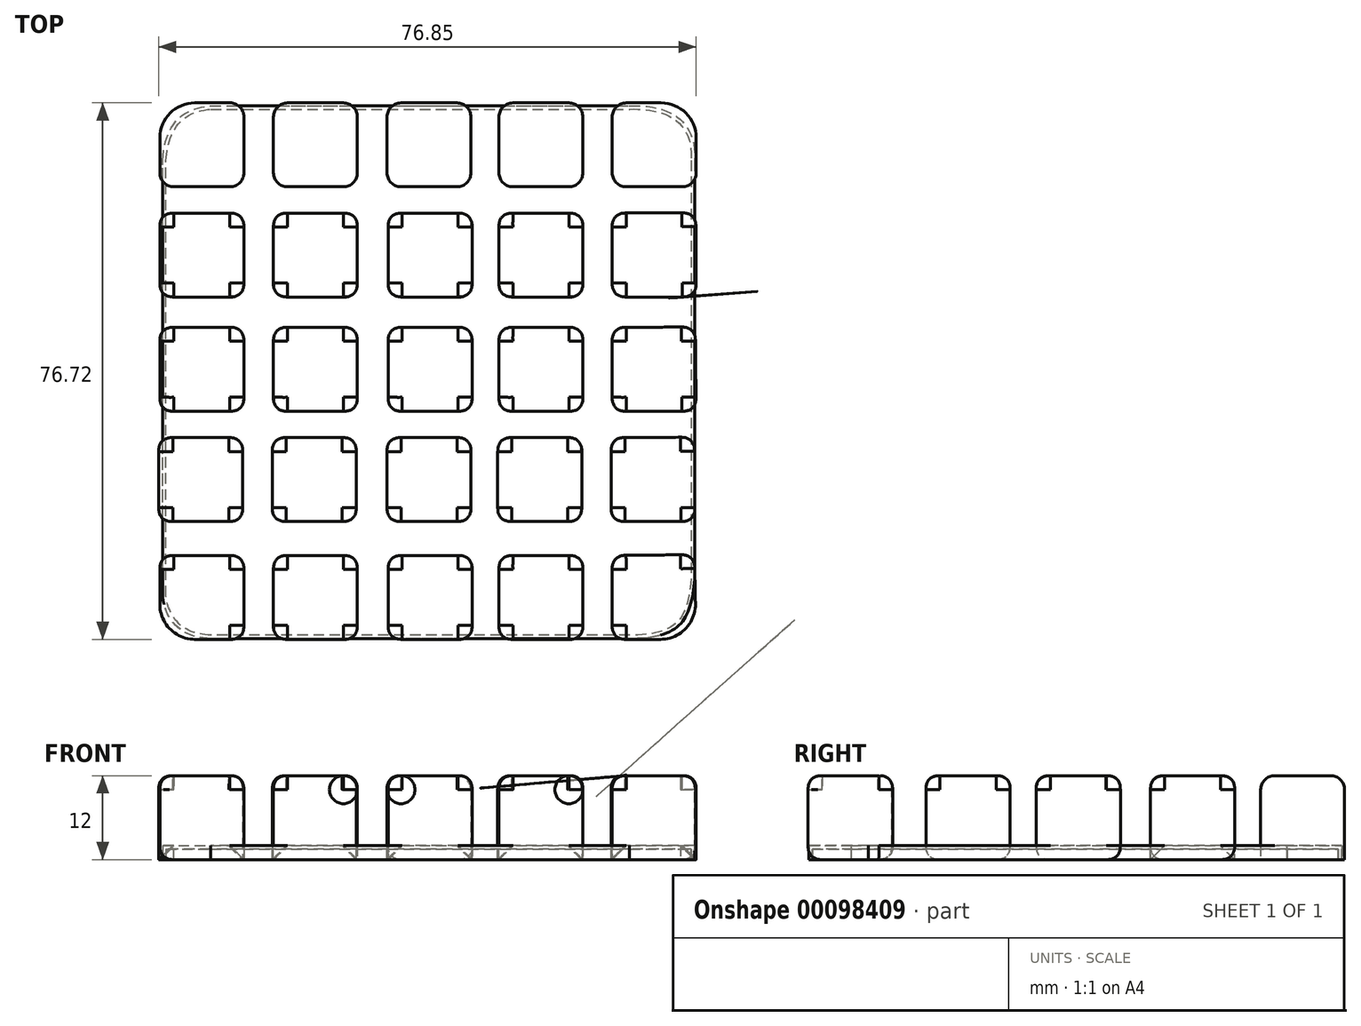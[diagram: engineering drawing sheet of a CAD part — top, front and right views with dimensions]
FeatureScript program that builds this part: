
annotation { "Feature Type Name" : "Feature", "Feature Type Description" : "" }
export const myFeature = defineFeature(function(context is Context, id is Id, definition is map)
    precondition{}
    {
        {
            var Q0;
            Q0=qCreatedBy(makeId("Top.planeOp"),FACE);
            var sketch = newSketch(context, id + "F0", { "sketchPlane" : qUnion([Q0]), "disableImprinting" : false});
            skFitSpline(sketch, "E0", {"points": [v(-42.78, 33) * mm, v(-35.9, 40.85) * mm], "startDerivative": vector(1.12, 17.42) * mm, "endDerivative": vector(10.47, 1.03) * mm});
            skFitSpline(sketch, "E1", {"points": [v(-35.9, 40.85) * mm, v(24.01, 40.85) * mm], "startDerivative": vector(59.63, 0) * mm, "endDerivative": vector(59.63, 0) * mm});
            skFitSpline(sketch, "E2", {"points": [v(24.01, 40.85) * mm, v(33.3, 33) * mm], "startDerivative": vector(21.28, 0.62) * mm, "endDerivative": vector(-0.8, -13.72) * mm});
            skFitSpline(sketch, "E3", {"points": [v(33.3, 33) * mm, v(33.3, -26.83) * mm], "startDerivative": vector(0, -59.82) * mm, "endDerivative": vector(0, -59.82) * mm});
            skFitSpline(sketch, "E4", {"points": [v(33.3, -26.83) * mm, v(24.01, -35.35) * mm], "startDerivative": vector(-1.47, -16.8) * mm, "endDerivative": vector(-22.63, 0.24) * mm});
            skFitSpline(sketch, "E5", {"points": [v(24.01, -35.35) * mm, v(-35.9, -35.35) * mm], "startDerivative": vector(-59.63, 0) * mm, "endDerivative": vector(-59.63, 0) * mm});
            skFitSpline(sketch, "E6", {"points": [v(-35.9, -35.35) * mm, v(-42.78, -29.35) * mm], "startDerivative": vector(-12.8, 0.34) * mm, "endDerivative": vector(-1.44, 10.4) * mm});
            skFitSpline(sketch, "E7", {"points": [v(-42.78, -29.35) * mm, v(-42.78, 33) * mm], "startDerivative": vector(0, 62.34) * mm, "endDerivative": vector(0, 62.34) * mm});
            skLineSegment(sketch, "E8", {"start": v(10.14, 40.85) * mm, "end": v(10.14, -35.35) * mm, "construction": true});
            skSolve(sketch);
        }
        {
            var Q0;
            Q0 = qSketchRegion(id + "F0", true);
            extrude(context, id + "F1", {"entities" : qUnion([Q0]), "depth" : 2 * mm, "offsetDistance" : 25 * mm});
        }
        {
            var Q0;
            Q0=makeQuery(id+"FE2RlGiIe2qTgEf_1.opExtrude","CAP_FACE",FACE,{"disambiguationData":[OSD([sQuery(id+"F0.wireOp",EDGE,"E0"),sQuery(id+"F0.wireOp",EDGE,"E1"),sQuery(id+"F0.wireOp",EDGE,"E2"),sQuery(id+"F0.wireOp",EDGE,"E3"),sQuery(id+"F0.wireOp",EDGE,"E4"),sQuery(id+"F0.wireOp",EDGE,"E5"),sQuery(id+"F0.wireOp",EDGE,"E6"),sQuery(id+"F0.wireOp",EDGE,"E7")])],"isStart":false});
            var Q1;
            Q1=makeQuery(id+"F1.opExtrude","CAP_FACE",FACE,{"disambiguationData":[OSD([sQuery(id+"F0.wireOp",EDGE,"E0"),sQuery(id+"F0.wireOp",EDGE,"E1"),sQuery(id+"F0.wireOp",EDGE,"E2"),sQuery(id+"F0.wireOp",EDGE,"E3"),sQuery(id+"F0.wireOp",EDGE,"E4"),sQuery(id+"F0.wireOp",EDGE,"E5"),sQuery(id+"F0.wireOp",EDGE,"E6"),sQuery(id+"F0.wireOp",EDGE,"E7")])],"isStart":true});
            shell(context, id + "F2", {"entities" : qUnion([Q0, Q1]), "thickness" : 0.5 * mm});
        }
        {
            var Q0;
            Q0=qCreatedBy(makeId("Top.planeOp"),FACE);
            var sketch = newSketch(context, id + "F3", { "sketchPlane" : qUnion([Q0]), "disableImprinting" : false});
            skLineSegment(sketch, "E9.bottom", {"start": v(-38.15, 41.25) * mm, "end": v(-31.13, 41.25) * mm});
            skLineSegment(sketch, "E9.top", {"start": v(-43.15, 29.25) * mm, "end": v(-31.13, 29.25) * mm});
            skLineSegment(sketch, "E9.left", {"start": v(-43.15, 36.25) * mm, "end": v(-43.15, 29.25) * mm});
            skLineSegment(sketch, "E9.right", {"start": v(-31.13, 41.25) * mm, "end": v(-31.13, 29.25) * mm});
            skLineSegment(sketch, "E10.1.0.0", {"start": v(-26.91, 41.25) * mm, "end": v(-14.91, 41.25) * mm});
            skLineSegment(sketch, "E10.1.0.1", {"start": v(-14.91, 41.25) * mm, "end": v(-14.91, 29.25) * mm});
            skLineSegment(sketch, "E10.1.0.2", {"start": v(-26.91, 29.25) * mm, "end": v(-14.91, 29.25) * mm});
            skLineSegment(sketch, "E10.1.0.3", {"start": v(-26.91, 41.25) * mm, "end": v(-26.91, 29.25) * mm});
            skLineSegment(sketch, "E10.2.0.0", {"start": v(-10.67, 41.25) * mm, "end": v(1.33, 41.25) * mm});
            skLineSegment(sketch, "E10.2.0.1", {"start": v(1.33, 41.25) * mm, "end": v(1.33, 29.25) * mm});
            skLineSegment(sketch, "E10.2.0.2", {"start": v(-10.67, 29.25) * mm, "end": v(1.33, 29.25) * mm});
            skLineSegment(sketch, "E10.2.0.3", {"start": v(-10.67, 41.25) * mm, "end": v(-10.67, 29.25) * mm});
            skLineSegment(sketch, "E10.3.0.0", {"start": v(5.33, 41.25) * mm, "end": v(17.33, 41.25) * mm});
            skLineSegment(sketch, "E10.3.0.1", {"start": v(17.33, 41.25) * mm, "end": v(17.33, 29.25) * mm});
            skLineSegment(sketch, "E10.3.0.2", {"start": v(5.33, 29.25) * mm, "end": v(17.33, 29.25) * mm});
            skLineSegment(sketch, "E10.3.0.3", {"start": v(5.33, 41.25) * mm, "end": v(5.33, 29.25) * mm});
            skLineSegment(sketch, "E10.4.0.0", {"start": v(21.53, 41.25) * mm, "end": v(28.53, 41.25) * mm});
            skLineSegment(sketch, "E10.4.0.1", {"start": v(33.53, 36.25) * mm, "end": v(33.53, 29.25) * mm});
            skLineSegment(sketch, "E10.4.0.2", {"start": v(21.53, 29.25) * mm, "end": v(33.53, 29.25) * mm});
            skLineSegment(sketch, "E10.4.0.3", {"start": v(21.53, 41.25) * mm, "end": v(21.53, 29.25) * mm});
            skPoint(sketch, "E11.visualSharp", {"position": v(35.33, 41.25) * mm});
            skArc(sketch, "E11.filletArc", {"start": v(33.53, 36.25) * mm, "mid": v(32.06, 39.79) * mm, "end": v(28.53, 41.25) * mm});
            skLineSegment(sketch, "E12.bottom", {"start": v(-43.15, 25.5) * mm, "end": v(-31.15, 25.5) * mm});
            skLineSegment(sketch, "E12.top", {"start": v(-43.15, 13.5) * mm, "end": v(-31.15, 13.5) * mm});
            skLineSegment(sketch, "E12.left", {"start": v(-43.15, 25.5) * mm, "end": v(-43.15, 13.5) * mm});
            skLineSegment(sketch, "E12.right", {"start": v(-31.15, 25.5) * mm, "end": v(-31.15, 13.5) * mm});
            skLineSegment(sketch, "E13.1.0.0", {"start": v(-26.91, 25.5) * mm, "end": v(-14.91, 25.5) * mm});
            skLineSegment(sketch, "E13.1.0.1", {"start": v(-14.91, 25.5) * mm, "end": v(-14.91, 13.5) * mm});
            skLineSegment(sketch, "E13.1.0.2", {"start": v(-26.91, 13.5) * mm, "end": v(-14.91, 13.5) * mm});
            skLineSegment(sketch, "E13.1.0.3", {"start": v(-26.91, 25.5) * mm, "end": v(-26.91, 13.5) * mm});
            skLineSegment(sketch, "E13.2.0.0", {"start": v(-10.51, 25.5) * mm, "end": v(1.49, 25.5) * mm});
            skLineSegment(sketch, "E13.2.0.1", {"start": v(1.49, 25.5) * mm, "end": v(1.49, 13.5) * mm});
            skLineSegment(sketch, "E13.2.0.2", {"start": v(-10.51, 13.5) * mm, "end": v(1.49, 13.5) * mm});
            skLineSegment(sketch, "E13.2.0.3", {"start": v(-10.51, 25.5) * mm, "end": v(-10.51, 13.5) * mm});
            skLineSegment(sketch, "E13.3.0.0", {"start": v(5.33, 25.5) * mm, "end": v(17.33, 25.5) * mm});
            skLineSegment(sketch, "E13.3.0.1", {"start": v(17.33, 25.5) * mm, "end": v(17.33, 13.5) * mm});
            skLineSegment(sketch, "E13.3.0.2", {"start": v(5.33, 13.5) * mm, "end": v(17.33, 13.5) * mm});
            skLineSegment(sketch, "E13.3.0.3", {"start": v(5.33, 25.5) * mm, "end": v(5.33, 13.5) * mm});
            skLineSegment(sketch, "E13.4.0.0", {"start": v(21.53, 25.5) * mm, "end": v(33.48, 25.53) * mm});
            skLineSegment(sketch, "E13.4.0.1", {"start": v(33.48, 25.53) * mm, "end": v(33.53, 13.5) * mm});
            skLineSegment(sketch, "E13.4.0.2", {"start": v(21.53, 13.5) * mm, "end": v(33.53, 13.5) * mm});
            skLineSegment(sketch, "E13.4.0.3", {"start": v(21.53, 25.5) * mm, "end": v(21.53, 13.5) * mm});
            skLineSegment(sketch, "E14.bottom", {"start": v(-43.15, 9.15) * mm, "end": v(-31.15, 9.15) * mm});
            skLineSegment(sketch, "E14.top", {"start": v(-43.15, -2.85) * mm, "end": v(-31.15, -2.85) * mm});
            skLineSegment(sketch, "E14.left", {"start": v(-43.15, 9.15) * mm, "end": v(-43.15, -2.85) * mm});
            skLineSegment(sketch, "E14.right", {"start": v(-31.15, 9.15) * mm, "end": v(-31.15, -2.85) * mm});
            skLineSegment(sketch, "E15.1.0.0", {"start": v(-26.91, 9.15) * mm, "end": v(-14.91, 9.15) * mm});
            skLineSegment(sketch, "E15.1.0.1", {"start": v(-14.91, 9.15) * mm, "end": v(-14.91, -2.85) * mm});
            skLineSegment(sketch, "E15.1.0.2", {"start": v(-26.91, -2.85) * mm, "end": v(-14.91, -2.85) * mm});
            skLineSegment(sketch, "E15.1.0.3", {"start": v(-26.91, 9.15) * mm, "end": v(-26.91, -2.85) * mm});
            skLineSegment(sketch, "E15.2.0.0", {"start": v(-10.51, 9.15) * mm, "end": v(1.49, 9.15) * mm});
            skLineSegment(sketch, "E15.2.0.1", {"start": v(1.49, 9.15) * mm, "end": v(1.49, -2.85) * mm});
            skLineSegment(sketch, "E15.2.0.2", {"start": v(-10.51, -2.85) * mm, "end": v(1.49, -2.85) * mm});
            skLineSegment(sketch, "E15.2.0.3", {"start": v(-10.51, 9.15) * mm, "end": v(-10.51, -2.85) * mm});
            skLineSegment(sketch, "E15.3.0.0", {"start": v(5.33, 9.15) * mm, "end": v(17.33, 9.15) * mm});
            skLineSegment(sketch, "E15.3.0.1", {"start": v(17.33, 9.15) * mm, "end": v(17.33, -2.85) * mm});
            skLineSegment(sketch, "E15.3.0.2", {"start": v(5.33, -2.85) * mm, "end": v(17.33, -2.85) * mm});
            skLineSegment(sketch, "E15.3.0.3", {"start": v(5.33, 9.15) * mm, "end": v(5.33, -2.85) * mm});
            skLineSegment(sketch, "E15.4.0.0", {"start": v(21.53, 9.15) * mm, "end": v(33.4, 9.2) * mm});
            skLineSegment(sketch, "E15.4.0.1", {"start": v(33.4, 9.2) * mm, "end": v(33.53, -2.85) * mm});
            skLineSegment(sketch, "E15.4.0.2", {"start": v(21.53, -2.85) * mm, "end": v(33.53, -2.85) * mm});
            skLineSegment(sketch, "E15.4.0.3", {"start": v(21.53, 9.15) * mm, "end": v(21.53, -2.85) * mm});
            skLineSegment(sketch, "E16.bottom", {"start": v(-43.31, -6.62) * mm, "end": v(-31.31, -6.62) * mm});
            skLineSegment(sketch, "E16.top", {"start": v(-43.31, -18.62) * mm, "end": v(-31.31, -18.62) * mm});
            skLineSegment(sketch, "E16.left", {"start": v(-43.31, -6.62) * mm, "end": v(-43.31, -18.62) * mm});
            skLineSegment(sketch, "E16.right", {"start": v(-31.31, -6.62) * mm, "end": v(-31.31, -18.62) * mm});
            skLineSegment(sketch, "E17.1.0.0", {"start": v(-27.07, -6.62) * mm, "end": v(-15.07, -6.62) * mm});
            skLineSegment(sketch, "E17.1.0.1", {"start": v(-15.07, -6.62) * mm, "end": v(-15.07, -18.62) * mm});
            skLineSegment(sketch, "E17.1.0.2", {"start": v(-27.07, -18.62) * mm, "end": v(-15.07, -18.62) * mm});
            skLineSegment(sketch, "E17.1.0.3", {"start": v(-27.07, -6.62) * mm, "end": v(-27.07, -18.62) * mm});
            skLineSegment(sketch, "E17.2.0.0", {"start": v(-10.67, -6.62) * mm, "end": v(1.33, -6.62) * mm});
            skLineSegment(sketch, "E17.2.0.1", {"start": v(1.33, -6.62) * mm, "end": v(1.33, -18.62) * mm});
            skLineSegment(sketch, "E17.2.0.2", {"start": v(-10.67, -18.62) * mm, "end": v(1.33, -18.62) * mm});
            skLineSegment(sketch, "E17.2.0.3", {"start": v(-10.67, -6.62) * mm, "end": v(-10.67, -18.62) * mm});
            skLineSegment(sketch, "E17.3.0.0", {"start": v(5.16, -6.62) * mm, "end": v(17.16, -6.62) * mm});
            skLineSegment(sketch, "E17.3.0.1", {"start": v(17.16, -6.62) * mm, "end": v(17.16, -18.62) * mm});
            skLineSegment(sketch, "E17.3.0.2", {"start": v(5.16, -18.62) * mm, "end": v(17.16, -18.62) * mm});
            skLineSegment(sketch, "E17.3.0.3", {"start": v(5.16, -6.62) * mm, "end": v(5.16, -18.62) * mm});
            skLineSegment(sketch, "E17.4.0.0", {"start": v(21.36, -6.62) * mm, "end": v(33.28, -6.56) * mm});
            skLineSegment(sketch, "E17.4.0.1", {"start": v(33.28, -6.56) * mm, "end": v(33.36, -18.62) * mm});
            skLineSegment(sketch, "E17.4.0.2", {"start": v(21.36, -18.62) * mm, "end": v(33.36, -18.62) * mm});
            skLineSegment(sketch, "E17.4.0.3", {"start": v(21.36, -6.62) * mm, "end": v(21.36, -18.62) * mm});
            skLineSegment(sketch, "E18.bottom", {"start": v(-43.15, -23.47) * mm, "end": v(-31.15, -23.47) * mm});
            skLineSegment(sketch, "E18.top", {"start": v(-38.15, -35.47) * mm, "end": v(-31.15, -35.47) * mm});
            skLineSegment(sketch, "E18.left", {"start": v(-43.15, -23.47) * mm, "end": v(-43.15, -30.47) * mm});
            skLineSegment(sketch, "E18.right", {"start": v(-31.15, -23.47) * mm, "end": v(-31.15, -35.47) * mm});
            skLineSegment(sketch, "E19.1.0.0", {"start": v(-26.91, -23.47) * mm, "end": v(-14.91, -23.47) * mm});
            skLineSegment(sketch, "E19.1.0.1", {"start": v(-14.91, -23.47) * mm, "end": v(-14.91, -35.47) * mm});
            skLineSegment(sketch, "E19.1.0.2", {"start": v(-26.91, -35.47) * mm, "end": v(-14.91, -35.47) * mm});
            skLineSegment(sketch, "E19.1.0.3", {"start": v(-26.91, -23.47) * mm, "end": v(-26.91, -35.47) * mm});
            skLineSegment(sketch, "E19.2.0.0", {"start": v(-10.51, -23.47) * mm, "end": v(1.49, -23.47) * mm});
            skLineSegment(sketch, "E19.2.0.1", {"start": v(1.49, -23.47) * mm, "end": v(1.49, -35.47) * mm});
            skLineSegment(sketch, "E19.2.0.2", {"start": v(-10.51, -35.47) * mm, "end": v(1.49, -35.47) * mm});
            skLineSegment(sketch, "E19.2.0.3", {"start": v(-10.51, -23.47) * mm, "end": v(-10.51, -35.47) * mm});
            skLineSegment(sketch, "E19.3.0.0", {"start": v(5.33, -23.47) * mm, "end": v(17.33, -23.47) * mm});
            skLineSegment(sketch, "E19.3.0.1", {"start": v(17.33, -23.47) * mm, "end": v(17.33, -35.47) * mm});
            skLineSegment(sketch, "E19.3.0.2", {"start": v(5.33, -35.47) * mm, "end": v(17.33, -35.47) * mm});
            skLineSegment(sketch, "E19.3.0.3", {"start": v(5.33, -23.47) * mm, "end": v(5.33, -35.47) * mm});
            skLineSegment(sketch, "E19.4.0.0", {"start": v(21.53, -23.47) * mm, "end": v(33.28, -23.36) * mm});
            skLineSegment(sketch, "E19.4.0.1", {"start": v(33.28, -23.36) * mm, "end": v(33.42, -30.37) * mm});
            skLineSegment(sketch, "E19.4.0.2", {"start": v(21.53, -35.47) * mm, "end": v(28.42, -35.47) * mm});
            skLineSegment(sketch, "E19.4.0.3", {"start": v(21.53, -23.47) * mm, "end": v(21.53, -35.47) * mm});
            skPoint(sketch, "E20.newPointA", {"position": v(-44.7, 41.25) * mm});
            skPoint(sketch, "E20.newPointB", {"position": v(-44.7, 41.25) * mm});
            skArc(sketch, "E20.filletArc", {"start": v(-38.15, 41.25) * mm, "mid": v(-41.69, 39.79) * mm, "end": v(-43.15, 36.25) * mm});
            skPoint(sketch, "E21.visualSharp", {"position": v(-44.51, -35.47) * mm});
            skArc(sketch, "E21.filletArc", {"start": v(-43.15, -30.47) * mm, "mid": v(-41.69, -34) * mm, "end": v(-38.15, -35.47) * mm});
            skPoint(sketch, "E22.visualSharp", {"position": v(33.53, -35.47) * mm});
            skArc(sketch, "E22.filletArc", {"start": v(28.42, -35.47) * mm, "mid": v(32, -33.97) * mm, "end": v(33.42, -30.37) * mm});
            skLineSegment(sketch, "E23", {"start": v(-48.6, 32.93) * mm, "end": v(-43.15, 32.93) * mm, "construction": true});
            skSolve(sketch);
        }
        {
            var Q0;
            Q0 = qSketchRegion(id + "F3", true);
            extrude(context, id + "F4", {"entities" : qUnion([Q0]), "depth" : 12 * mm, "offsetDistance" : 25 * mm});
        }
        {
            var Q0;
            Q0=makeQuery(id+"F4.opExtrude","CAP_EDGE",EDGE,{"disambiguationData":[OSD([sQuery(id+"F3.wireOp",EDGE,"E10.2.0.3")])],"isStart":false});
            var Q1;
            Q1=makeQuery(id+"F4.opExtrude","CAP_EDGE",EDGE,{"disambiguationData":[OSD([sQuery(id+"F3.wireOp",EDGE,"E10.2.0.1")])],"isStart":false});
            var Q2;
            Q2=makeQuery(id+"F4.opExtrude","CAP_EDGE",EDGE,{"disambiguationData":[OSD([sQuery(id+"F3.wireOp",EDGE,"E10.1.0.1")])],"isStart":false});
            var Q3;
            Q3=makeQuery(id+"F4.opExtrude","CAP_EDGE",EDGE,{"disambiguationData":[OSD([sQuery(id+"F3.wireOp",EDGE,"E10.1.0.3")])],"isStart":false});
            var Q4;
            Q4=makeQuery(id+"F4.opExtrude","CAP_EDGE",EDGE,{"disambiguationData":[OSD([sQuery(id+"F3.wireOp",EDGE,"E10.3.0.3")])],"isStart":false});
            var Q5;
            Q5=makeQuery(id+"F4.opExtrude","CAP_EDGE",EDGE,{"disambiguationData":[OSD([sQuery(id+"F3.wireOp",EDGE,"E10.3.0.1")])],"isStart":false});
            var Q6;
            Q6=makeQuery(id+"F4.opExtrude","CAP_EDGE",EDGE,{"disambiguationData":[OSD([sQuery(id+"F3.wireOp",EDGE,"E9.right")])],"isStart":false});
            var Q7;
            Q7=makeQuery(id+"F4.opExtrude","CAP_EDGE",EDGE,{"disambiguationData":[OSD([sQuery(id+"F3.wireOp",EDGE,"E10.4.0.3")])],"isStart":false});
            var Q8;
            Q8=makeQuery(id+"F4.opExtrude","CAP_EDGE",EDGE,{"disambiguationData":[OSD([sQuery(id+"F3.wireOp",EDGE,"E9.left")])],"isStart":false});
            var Q9;
            Q9=makeQuery(id+"F4.opExtrude","CAP_EDGE",EDGE,{"disambiguationData":[OSD([sQuery(id+"F3.wireOp",EDGE,"E10.4.0.1")])],"isStart":false});
            fillet(context, id + "F5", {"entities" : qUnion([Q0, Q1, Q2, Q3, Q4, Q5, Q6, Q7, Q8, Q9]), "tangentPropagation" : true, "radius" : 2 * mm, "defaultsChanged" : false, "vertexSettings" : [], "allowEdgeOverflow" : false});
        }
        {
            var Q0;
            Q0=makeQuery(id+"F4.opExtrude","CAP_EDGE",EDGE,{"disambiguationData":[OSD([sQuery(id+"F3.wireOp",EDGE,"E9.top")])],"isStart":false});
            fillet(context, id + "F6", {"entities" : qUnion([Q0]), "tangentPropagation" : true, "radius" : 2 * mm, "defaultsChanged" : true, "vertexSettings" : [], "allowEdgeOverflow" : false});
        }
        {
            var Q0;
            Q0=makeQuery(id+"F4.opExtrude","CAP_EDGE",EDGE,{"disambiguationData":[OSD([sQuery(id+"F3.wireOp",EDGE,"E10.1.0.2")])],"isStart":false});
            var Q1;
            Q1=makeQuery(id+"F4.opExtrude","CAP_EDGE",EDGE,{"disambiguationData":[OSD([sQuery(id+"F3.wireOp",EDGE,"E10.2.0.2")])],"isStart":false});
            var Q2;
            Q2=makeQuery(id+"F5.opFillet","BLEND_EDGE",EDGE,{"blendedFrom":[makeQuery(id+"F4.opExtrude","CAP_EDGE",EDGE,{"disambiguationData":[OSD([sQuery(id+"F3.wireOp",EDGE,"E10.1.0.1")])],"isStart":false}),makeQuery(id+"F4.opExtrude","SWEPT_FACE",FACE,{"disambiguationData":[OSD([sQuery(id+"F3.wireOp",EDGE,"E10.1.0.2")])]})],"blendedInto":[makeQuery(id+"F4.opExtrude","SWEPT_FACE",FACE,{"disambiguationData":[OSD([sQuery(id+"F3.wireOp",EDGE,"E10.1.0.2")])]})]});
            var Q3;
            Q3=makeQuery(id+"F5.opFillet","BLEND_EDGE",EDGE,{"blendedFrom":[makeQuery(id+"F4.opExtrude","CAP_EDGE",EDGE,{"disambiguationData":[OSD([sQuery(id+"F3.wireOp",EDGE,"E10.1.0.3")])],"isStart":false}),makeQuery(id+"F4.opExtrude","SWEPT_FACE",FACE,{"disambiguationData":[OSD([sQuery(id+"F3.wireOp",EDGE,"E10.1.0.2")])]})],"blendedInto":[makeQuery(id+"F4.opExtrude","SWEPT_FACE",FACE,{"disambiguationData":[OSD([sQuery(id+"F3.wireOp",EDGE,"E10.1.0.2")])]})]});
            var Q4;
            Q4=makeQuery(id+"F4.opExtrude","CAP_EDGE",EDGE,{"disambiguationData":[OSD([sQuery(id+"F3.wireOp",EDGE,"E10.1.0.0")])],"isStart":false});
            var Q5;
            Q5=makeQuery(id+"F4.opExtrude","CAP_EDGE",EDGE,{"disambiguationData":[OSD([sQuery(id+"F3.wireOp",EDGE,"E10.2.0.0")])],"isStart":false});
            var Q6;
            Q6=makeQuery(id+"F4.opExtrude","CAP_EDGE",EDGE,{"disambiguationData":[OSD([sQuery(id+"F3.wireOp",EDGE,"E10.3.0.0")])],"isStart":false});
            var Q7;
            Q7=makeQuery(id+"F4.opExtrude","CAP_EDGE",EDGE,{"disambiguationData":[OSD([sQuery(id+"F3.wireOp",EDGE,"E10.3.0.2")])],"isStart":false});
            var Q8;
            Q8=makeQuery(id+"F4.opExtrude","CAP_EDGE",EDGE,{"disambiguationData":[OSD([sQuery(id+"F3.wireOp",EDGE,"E10.4.0.2")])],"isStart":false});
            var Q9;
            {var subQ0=sQuery(id+"F3.wireOp",EDGE,"E10.4.0.0");Q9=makeQuery(id+"F5.opFillet","BLEND_EDGE",EDGE,{"blendedFrom":[makeQuery(id+"F4.opExtrude","CAP_EDGE",EDGE,{"disambiguationData":[OSD([subQ0])],"isStart":false}),makeQuery(id+"F4.opExtrude","CAP_FACE",FACE,{"disambiguationData":[OSD([subQ0,sQuery(id+"F3.wireOp",EDGE,"E10.4.0.1"),sQuery(id+"F3.wireOp",EDGE,"E10.4.0.2"),sQuery(id+"F3.wireOp",EDGE,"E10.4.0.3"),sQuery(id+"F3.wireOp",EDGE,"E11.filletArc")])],"isStart":false})],"blendedInto":[makeQuery(id+"F4.opExtrude","CAP_FACE",FACE,{"disambiguationData":[OSD([subQ0,sQuery(id+"F3.wireOp",EDGE,"E10.4.0.1"),sQuery(id+"F3.wireOp",EDGE,"E10.4.0.2"),sQuery(id+"F3.wireOp",EDGE,"E10.4.0.3"),sQuery(id+"F3.wireOp",EDGE,"E11.filletArc")])],"isStart":false})]});}
            var Q10;
            Q10=makeQuery(id+"F5.opFillet","BLEND_FACE",FACE,{"disambiguationData":[OSD([sQuery(id+"F3.wireOp",EDGE,"E10.4.0.0")])]});
            var Q11;
            Q11=makeQuery(id+"F5.opFillet","BLEND_FACE",FACE,{"disambiguationData":[OSD([sQuery(id+"F3.wireOp",EDGE,"E9.bottom")])]});
            fillet(context, id + "F7", {"entities" : qUnion([Q0, Q1, Q2, Q3, Q4, Q5, Q6, Q7, Q8, Q9, Q10, Q11]), "tangentPropagation" : true, "radius" : 2 * mm, "defaultsChanged" : false, "vertexSettings" : [], "allowEdgeOverflow" : false});
        }
        {
            var Q0;
            Q0=makeQuery(id+"F4.opExtrude","CAP_EDGE",EDGE,{"disambiguationData":[OSD([sQuery(id+"F3.wireOp",EDGE,"E13.1.0.0")])],"isStart":false});
            var Q1;
            Q1=makeQuery(id+"F4.opExtrude","CAP_EDGE",EDGE,{"disambiguationData":[OSD([sQuery(id+"F3.wireOp",EDGE,"E13.1.0.1")])],"isStart":false});
            var Q2;
            Q2=makeQuery(id+"F4.opExtrude","CAP_EDGE",EDGE,{"disambiguationData":[OSD([sQuery(id+"F3.wireOp",EDGE,"E13.1.0.2")])],"isStart":false});
            var Q3;
            Q3=makeQuery(id+"F4.opExtrude","CAP_EDGE",EDGE,{"disambiguationData":[OSD([sQuery(id+"F3.wireOp",EDGE,"E13.1.0.3")])],"isStart":false});
            var Q4;
            Q4=makeQuery(id+"F4.opExtrude","SWEPT_FACE",FACE,{"disambiguationData":[OSD([sQuery(id+"F3.wireOp",EDGE,"E13.1.0.0")])]});
            var Q5;
            Q5=makeQuery(id+"F4.opExtrude","SWEPT_FACE",FACE,{"disambiguationData":[OSD([sQuery(id+"F3.wireOp",EDGE,"E13.1.0.2")])]});
            var Q6;
            Q6=makeQuery(id+"F4.opExtrude","CAP_EDGE",EDGE,{"disambiguationData":[OSD([sQuery(id+"F3.wireOp",EDGE,"E13.2.0.2")])],"isStart":false});
            var Q7;
            Q7=makeQuery(id+"F4.opExtrude","CAP_EDGE",EDGE,{"disambiguationData":[OSD([sQuery(id+"F3.wireOp",EDGE,"E13.2.0.1")])],"isStart":false});
            var Q8;
            Q8=makeQuery(id+"F4.opExtrude","CAP_EDGE",EDGE,{"disambiguationData":[OSD([sQuery(id+"F3.wireOp",EDGE,"E13.2.0.0")])],"isStart":false});
            var Q9;
            Q9=makeQuery(id+"F4.opExtrude","CAP_EDGE",EDGE,{"disambiguationData":[OSD([sQuery(id+"F3.wireOp",EDGE,"E13.2.0.3")])],"isStart":false});
            var Q10;
            Q10=makeQuery(id+"F4.opExtrude","SWEPT_FACE",FACE,{"disambiguationData":[OSD([sQuery(id+"F3.wireOp",EDGE,"E13.2.0.3")])]});
            var Q11;
            Q11=makeQuery(id+"F4.opExtrude","SWEPT_FACE",FACE,{"disambiguationData":[OSD([sQuery(id+"F3.wireOp",EDGE,"E13.2.0.1")])]});
            var Q12;
            Q12=makeQuery(id+"F4.opExtrude","CAP_FACE",FACE,{"disambiguationData":[OSD([sQuery(id+"F3.wireOp",EDGE,"E13.3.0.0"),sQuery(id+"F3.wireOp",EDGE,"E13.3.0.1"),sQuery(id+"F3.wireOp",EDGE,"E13.3.0.2"),sQuery(id+"F3.wireOp",EDGE,"E13.3.0.3")])],"isStart":false});
            var Q13;
            Q13=makeQuery(id+"F4.opExtrude","CAP_FACE",FACE,{"disambiguationData":[OSD([sQuery(id+"F3.wireOp",EDGE,"E13.4.0.0"),sQuery(id+"F3.wireOp",EDGE,"E13.4.0.1"),sQuery(id+"F3.wireOp",EDGE,"E13.4.0.2"),sQuery(id+"F3.wireOp",EDGE,"E13.4.0.3")])],"isStart":false});
            var Q14;
            Q14=makeQuery(id+"F4.opExtrude","CAP_FACE",FACE,{"disambiguationData":[OSD([sQuery(id+"F3.wireOp",EDGE,"E12.bottom"),sQuery(id+"F3.wireOp",EDGE,"E12.top"),sQuery(id+"F3.wireOp",EDGE,"E12.left"),sQuery(id+"F3.wireOp",EDGE,"E12.right")])],"isStart":false});
            var Q15;
            Q15=makeQuery(id+"F4.opExtrude","CAP_FACE",FACE,{"disambiguationData":[OSD([sQuery(id+"F3.wireOp",EDGE,"E14.bottom"),sQuery(id+"F3.wireOp",EDGE,"E14.top"),sQuery(id+"F3.wireOp",EDGE,"E14.left"),sQuery(id+"F3.wireOp",EDGE,"E14.right")])],"isStart":false});
            var Q16;
            Q16=makeQuery(id+"F4.opExtrude","CAP_FACE",FACE,{"disambiguationData":[OSD([sQuery(id+"F3.wireOp",EDGE,"E15.1.0.0"),sQuery(id+"F3.wireOp",EDGE,"E15.1.0.1"),sQuery(id+"F3.wireOp",EDGE,"E15.1.0.2"),sQuery(id+"F3.wireOp",EDGE,"E15.1.0.3")])],"isStart":false});
            var Q17;
            Q17=makeQuery(id+"F4.opExtrude","CAP_FACE",FACE,{"disambiguationData":[OSD([sQuery(id+"F3.wireOp",EDGE,"E15.2.0.0"),sQuery(id+"F3.wireOp",EDGE,"E15.2.0.1"),sQuery(id+"F3.wireOp",EDGE,"E15.2.0.2"),sQuery(id+"F3.wireOp",EDGE,"E15.2.0.3")])],"isStart":false});
            var Q18;
            Q18=makeQuery(id+"F4.opExtrude","CAP_FACE",FACE,{"disambiguationData":[OSD([sQuery(id+"F3.wireOp",EDGE,"E15.3.0.0"),sQuery(id+"F3.wireOp",EDGE,"E15.3.0.1"),sQuery(id+"F3.wireOp",EDGE,"E15.3.0.2"),sQuery(id+"F3.wireOp",EDGE,"E15.3.0.3")])],"isStart":false});
            var Q19;
            Q19=makeQuery(id+"F4.opExtrude","CAP_FACE",FACE,{"disambiguationData":[OSD([sQuery(id+"F3.wireOp",EDGE,"E15.4.0.0"),sQuery(id+"F3.wireOp",EDGE,"E15.4.0.1"),sQuery(id+"F3.wireOp",EDGE,"E15.4.0.2"),sQuery(id+"F3.wireOp",EDGE,"E15.4.0.3")])],"isStart":false});
            var Q20;
            Q20=makeQuery(id+"F4.opExtrude","CAP_FACE",FACE,{"disambiguationData":[OSD([sQuery(id+"F3.wireOp",EDGE,"E17.4.0.0"),sQuery(id+"F3.wireOp",EDGE,"E17.4.0.1"),sQuery(id+"F3.wireOp",EDGE,"E17.4.0.2"),sQuery(id+"F3.wireOp",EDGE,"E17.4.0.3")])],"isStart":false});
            var Q21;
            Q21=makeQuery(id+"F4.opExtrude","CAP_FACE",FACE,{"disambiguationData":[OSD([sQuery(id+"F3.wireOp",EDGE,"E17.3.0.0"),sQuery(id+"F3.wireOp",EDGE,"E17.3.0.1"),sQuery(id+"F3.wireOp",EDGE,"E17.3.0.2"),sQuery(id+"F3.wireOp",EDGE,"E17.3.0.3")])],"isStart":false});
            var Q22;
            Q22=makeQuery(id+"F4.opExtrude","CAP_FACE",FACE,{"disambiguationData":[OSD([sQuery(id+"F3.wireOp",EDGE,"E17.2.0.0"),sQuery(id+"F3.wireOp",EDGE,"E17.2.0.1"),sQuery(id+"F3.wireOp",EDGE,"E17.2.0.2"),sQuery(id+"F3.wireOp",EDGE,"E17.2.0.3")])],"isStart":false});
            var Q23;
            Q23=makeQuery(id+"F4.opExtrude","CAP_FACE",FACE,{"disambiguationData":[OSD([sQuery(id+"F3.wireOp",EDGE,"E17.1.0.0"),sQuery(id+"F3.wireOp",EDGE,"E17.1.0.1"),sQuery(id+"F3.wireOp",EDGE,"E17.1.0.2"),sQuery(id+"F3.wireOp",EDGE,"E17.1.0.3")])],"isStart":false});
            var Q24;
            Q24=makeQuery(id+"F4.opExtrude","CAP_FACE",FACE,{"disambiguationData":[OSD([sQuery(id+"F3.wireOp",EDGE,"E16.bottom"),sQuery(id+"F3.wireOp",EDGE,"E16.top"),sQuery(id+"F3.wireOp",EDGE,"E16.left"),sQuery(id+"F3.wireOp",EDGE,"E16.right")])],"isStart":false});
            var Q25;
            Q25=makeQuery(id+"F4.opExtrude","CAP_FACE",FACE,{"disambiguationData":[OSD([sQuery(id+"F3.wireOp",EDGE,"E18.bottom"),sQuery(id+"F3.wireOp",EDGE,"E18.top"),sQuery(id+"F3.wireOp",EDGE,"E18.left"),sQuery(id+"F3.wireOp",EDGE,"E18.right"),sQuery(id+"F3.wireOp",EDGE,"E21.filletArc")])],"isStart":false});
            var Q26;
            Q26=makeQuery(id+"F4.opExtrude","CAP_FACE",FACE,{"disambiguationData":[OSD([sQuery(id+"F3.wireOp",EDGE,"E19.1.0.0"),sQuery(id+"F3.wireOp",EDGE,"E19.1.0.1"),sQuery(id+"F3.wireOp",EDGE,"E19.1.0.2"),sQuery(id+"F3.wireOp",EDGE,"E19.1.0.3")])],"isStart":false});
            var Q27;
            Q27=makeQuery(id+"F4.opExtrude","CAP_FACE",FACE,{"disambiguationData":[OSD([sQuery(id+"F3.wireOp",EDGE,"E19.2.0.0"),sQuery(id+"F3.wireOp",EDGE,"E19.2.0.1"),sQuery(id+"F3.wireOp",EDGE,"E19.2.0.2"),sQuery(id+"F3.wireOp",EDGE,"E19.2.0.3")])],"isStart":false});
            var Q28;
            Q28=makeQuery(id+"F4.opExtrude","CAP_FACE",FACE,{"disambiguationData":[OSD([sQuery(id+"F3.wireOp",EDGE,"E19.3.0.0"),sQuery(id+"F3.wireOp",EDGE,"E19.3.0.1"),sQuery(id+"F3.wireOp",EDGE,"E19.3.0.2"),sQuery(id+"F3.wireOp",EDGE,"E19.3.0.3")])],"isStart":false});
            var Q29;
            Q29=makeQuery(id+"F4.opExtrude","CAP_FACE",FACE,{"disambiguationData":[OSD([sQuery(id+"F3.wireOp",EDGE,"E19.4.0.0"),sQuery(id+"F3.wireOp",EDGE,"E19.4.0.1"),sQuery(id+"F3.wireOp",EDGE,"E19.4.0.2"),sQuery(id+"F3.wireOp",EDGE,"E19.4.0.3"),sQuery(id+"F3.wireOp",EDGE,"E22.filletArc")])],"isStart":false});
            var Q30;
            Q30=makeQuery(id+"F4.opExtrude","SWEPT_FACE",FACE,{"disambiguationData":[OSD([sQuery(id+"F3.wireOp",EDGE,"E12.top")])]});
            var Q31;
            Q31=makeQuery(id+"F4.opExtrude","SWEPT_FACE",FACE,{"disambiguationData":[OSD([sQuery(id+"F3.wireOp",EDGE,"E12.bottom")])]});
            var Q32;
            Q32=makeQuery(id+"F4.opExtrude","SWEPT_FACE",FACE,{"disambiguationData":[OSD([sQuery(id+"F3.wireOp",EDGE,"E13.3.0.2")])]});
            var Q33;
            Q33=makeQuery(id+"F4.opExtrude","SWEPT_FACE",FACE,{"disambiguationData":[OSD([sQuery(id+"F3.wireOp",EDGE,"E13.3.0.0")])]});
            var Q34;
            Q34=makeQuery(id+"F4.opExtrude","SWEPT_FACE",FACE,{"disambiguationData":[OSD([sQuery(id+"F3.wireOp",EDGE,"E13.4.0.0")])]});
            var Q35;
            Q35=makeQuery(id+"F4.opExtrude","SWEPT_FACE",FACE,{"disambiguationData":[OSD([sQuery(id+"F3.wireOp",EDGE,"E15.4.0.0")])]});
            var Q36;
            Q36=makeQuery(id+"F4.opExtrude","SWEPT_FACE",FACE,{"disambiguationData":[OSD([sQuery(id+"F3.wireOp",EDGE,"E15.3.0.0")])]});
            var Q37;
            Q37=makeQuery(id+"F4.opExtrude","SWEPT_FACE",FACE,{"disambiguationData":[OSD([sQuery(id+"F3.wireOp",EDGE,"E15.2.0.0")])]});
            var Q38;
            Q38=makeQuery(id+"F4.opExtrude","SWEPT_FACE",FACE,{"disambiguationData":[OSD([sQuery(id+"F3.wireOp",EDGE,"E15.1.0.0")])]});
            var Q39;
            Q39=makeQuery(id+"F4.opExtrude","SWEPT_FACE",FACE,{"disambiguationData":[OSD([sQuery(id+"F3.wireOp",EDGE,"E14.bottom")])]});
            var Q40;
            Q40=makeQuery(id+"F4.opExtrude","SWEPT_FACE",FACE,{"disambiguationData":[OSD([sQuery(id+"F3.wireOp",EDGE,"E13.4.0.2")])]});
            var Q41;
            Q41=makeQuery(id+"F4.opExtrude","SWEPT_FACE",FACE,{"disambiguationData":[OSD([sQuery(id+"F3.wireOp",EDGE,"E15.4.0.2")])]});
            var Q42;
            Q42=makeQuery(id+"F4.opExtrude","SWEPT_FACE",FACE,{"disambiguationData":[OSD([sQuery(id+"F3.wireOp",EDGE,"E15.3.0.2")])]});
            var Q43;
            Q43=makeQuery(id+"F4.opExtrude","SWEPT_FACE",FACE,{"disambiguationData":[OSD([sQuery(id+"F3.wireOp",EDGE,"E15.2.0.2")])]});
            var Q44;
            Q44=makeQuery(id+"F4.opExtrude","SWEPT_FACE",FACE,{"disambiguationData":[OSD([sQuery(id+"F3.wireOp",EDGE,"E15.1.0.2")])]});
            var Q45;
            Q45=makeQuery(id+"F4.opExtrude","SWEPT_FACE",FACE,{"disambiguationData":[OSD([sQuery(id+"F3.wireOp",EDGE,"E14.top")])]});
            var Q46;
            Q46=makeQuery(id+"F4.opExtrude","SWEPT_FACE",FACE,{"disambiguationData":[OSD([sQuery(id+"F3.wireOp",EDGE,"E16.top")])]});
            var Q47;
            Q47=makeQuery(id+"F4.opExtrude","SWEPT_FACE",FACE,{"disambiguationData":[OSD([sQuery(id+"F3.wireOp",EDGE,"E17.1.0.2")])]});
            var Q48;
            Q48=makeQuery(id+"F4.opExtrude","SWEPT_FACE",FACE,{"disambiguationData":[OSD([sQuery(id+"F3.wireOp",EDGE,"E17.2.0.2")])]});
            var Q49;
            Q49=makeQuery(id+"F4.opExtrude","SWEPT_FACE",FACE,{"disambiguationData":[OSD([sQuery(id+"F3.wireOp",EDGE,"E17.3.0.2")])]});
            var Q50;
            Q50=makeQuery(id+"F4.opExtrude","SWEPT_FACE",FACE,{"disambiguationData":[OSD([sQuery(id+"F3.wireOp",EDGE,"E17.4.0.2")])]});
            var Q51;
            Q51=makeQuery(id+"F4.opExtrude","SWEPT_FACE",FACE,{"disambiguationData":[OSD([sQuery(id+"F3.wireOp",EDGE,"E19.3.0.2")])]});
            var Q52;
            Q52=makeQuery(id+"F4.opExtrude","SWEPT_FACE",FACE,{"disambiguationData":[OSD([sQuery(id+"F3.wireOp",EDGE,"E19.2.0.2")])]});
            var Q53;
            Q53=makeQuery(id+"F4.opExtrude","SWEPT_FACE",FACE,{"disambiguationData":[OSD([sQuery(id+"F3.wireOp",EDGE,"E19.1.0.2")])]});
            var Q54;
            Q54=makeQuery(id+"F4.opExtrude","SWEPT_FACE",FACE,{"disambiguationData":[OSD([sQuery(id+"F3.wireOp",EDGE,"E17.4.0.0")])]});
            var Q55;
            Q55=makeQuery(id+"F4.opExtrude","SWEPT_FACE",FACE,{"disambiguationData":[OSD([sQuery(id+"F3.wireOp",EDGE,"E17.3.0.0")])]});
            var Q56;
            Q56=makeQuery(id+"F4.opExtrude","SWEPT_FACE",FACE,{"disambiguationData":[OSD([sQuery(id+"F3.wireOp",EDGE,"E17.2.0.0")])]});
            var Q57;
            Q57=makeQuery(id+"F4.opExtrude","SWEPT_FACE",FACE,{"disambiguationData":[OSD([sQuery(id+"F3.wireOp",EDGE,"E17.1.0.0")])]});
            var Q58;
            Q58=makeQuery(id+"F4.opExtrude","SWEPT_FACE",FACE,{"disambiguationData":[OSD([sQuery(id+"F3.wireOp",EDGE,"E16.bottom")])]});
            var Q59;
            Q59=makeQuery(id+"F4.opExtrude","SWEPT_FACE",FACE,{"disambiguationData":[OSD([sQuery(id+"F3.wireOp",EDGE,"E19.1.0.0")])]});
            var Q60;
            Q60=makeQuery(id+"F4.opExtrude","SWEPT_FACE",FACE,{"disambiguationData":[OSD([sQuery(id+"F3.wireOp",EDGE,"E19.2.0.0")])]});
            var Q61;
            Q61=makeQuery(id+"F4.opExtrude","SWEPT_FACE",FACE,{"disambiguationData":[OSD([sQuery(id+"F3.wireOp",EDGE,"E19.3.0.0")])]});
            var Q62;
            Q62=makeQuery(id+"F4.opExtrude","SWEPT_FACE",FACE,{"disambiguationData":[OSD([sQuery(id+"F3.wireOp",EDGE,"E19.4.0.0")])]});
            var Q63;
            Q63=makeQuery(id+"F4.opExtrude","SWEPT_FACE",FACE,{"disambiguationData":[OSD([sQuery(id+"F3.wireOp",EDGE,"E18.bottom")])]});
            var Q64;
            Q64=makeQuery(id+"F4.opExtrude","SWEPT_FACE",FACE,{"disambiguationData":[OSD([sQuery(id+"F3.wireOp",EDGE,"E18.top")])]});
            var Q65;
            Q65=makeQuery(id+"F4.opExtrude","SWEPT_FACE",FACE,{"disambiguationData":[OSD([sQuery(id+"F3.wireOp",EDGE,"E19.4.0.2")])]});
            fillet(context, id + "F8", {"entities" : qUnion([Q0, Q1, Q2, Q3, Q4, Q5, Q6, Q7, Q8, Q9, Q10, Q11, Q12, Q13, Q14, Q15, Q16, Q17, Q18, Q19, Q20, Q21, Q22, Q23, Q24, Q25, Q26, Q27, Q28, Q29, Q30, Q31, Q32, Q33, Q34, Q35, Q36, Q37, Q38, Q39, Q40, Q41, Q42, Q43, Q44, Q45, Q46, Q47, Q48, Q49, Q50, Q51, Q52, Q53, Q54, Q55, Q56, Q57, Q58, Q59, Q60, Q61, Q62, Q63, Q64, Q65]), "tangentPropagation" : true, "crossSection" : FilletCrossSection.CURVATURE, "radius" : 2 * mm, "magnitude" : 0.5, "defaultsChanged" : false, "vertexSettings" : []});
        }
        {
            var Q0;
            Q0=makeQuery(id+"F2.opShell","OFFSET_FACE",FACE,{"disambiguationData":[OSD([sQuery(id+"F0.wireOp",EDGE,"E0"),sQuery(id+"F0.wireOp",EDGE,"E1"),sQuery(id+"F0.wireOp",EDGE,"E2"),sQuery(id+"F0.wireOp",EDGE,"E3"),sQuery(id+"F0.wireOp",EDGE,"E4"),sQuery(id+"F0.wireOp",EDGE,"E5"),sQuery(id+"F0.wireOp",EDGE,"E6"),sQuery(id+"F0.wireOp",EDGE,"E7")])]});
            extrude(context, id + "F9", {"entities" : qUnion([Q0]), "depth" : 1.5 * mm, "offsetDistance" : 25 * mm});
        }
    });
